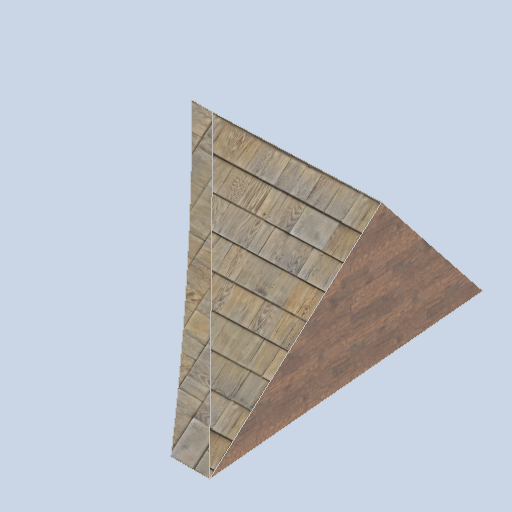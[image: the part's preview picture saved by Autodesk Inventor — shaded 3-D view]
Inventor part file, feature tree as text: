
AUTODESK INVENTOR PART (.ipt)
format: ipt  version: 2024.2 (Build 282272000, 272)  size: 257,536 bytes
history: native  units: in
note: dims shown in document units (in); Inventor stores cm internally (conversion verified against a paired STEP export)
features: sketch x6, plane x5, other x3
ambient origin geometry x8: Origin, YZ Plane, XZ Plane, XY Plane, X Axis, Y Axis, Z Axis, Center Point
bodies: Solid1 (feature_tree)
feature tree (14):
  other  "panel_pad_03_MIR.ipt"
  other  "Solid1::panel_pad_03_MIR.ipt"
  other  "TaggingFeature1"
  sketch  "Sketch1"  dims[d0=0.3937in]
  sketch  "Sketch2"
  sketch  "Sketch3"
  sketch  "Sketch6"
  sketch  "Sketch7"
  sketch  "Sketch8"
  plane  "Work Plane1"
  plane  "Work Plane2"
  plane  "Work Plane3"
  plane  "Work Plane4"
  plane  "Work Plane5"
